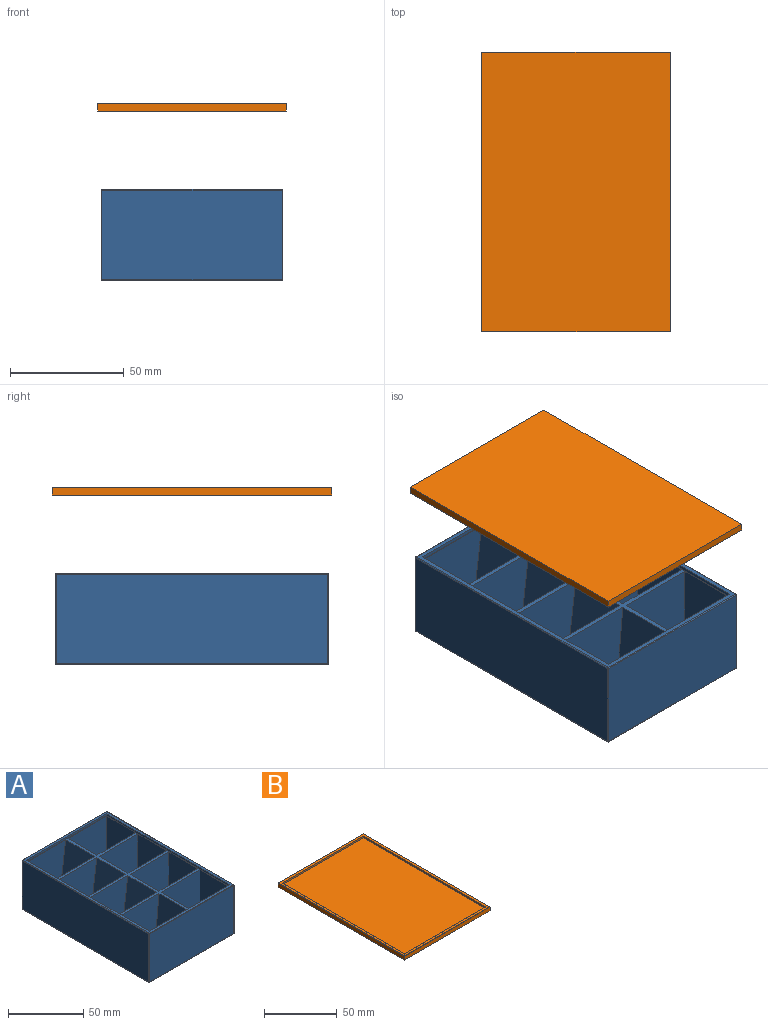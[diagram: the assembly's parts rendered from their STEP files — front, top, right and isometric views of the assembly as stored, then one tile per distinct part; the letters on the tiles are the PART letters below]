
ASSEMBLY  parts=2 mates=1
PART A: 81 faces, bbox 80x120x40 mm
  f0: plane 119.2x79.2mm, normal (0,0,1), area 701.3mm2, adj f9,f10,f19,f20,f27,f28,f29,f30
  f1: plane 79.2x39.2mm, normal (0,-1,0), area 3104.6mm2, adj f14,f19,f22,f25
  f2: plane 119.2x39.2mm, normal (1,0,0), area 4672.6mm2, adj f11,f20,f21,f25
  f3: plane 79.2x39.2mm, normal (0,1,0), area 3104.6mm2, adj f6,f10,f11,f12
  f4: plane 119.2x39.2mm, normal (-1,0,0), area 4672.6mm2, adj f6,f9,f13,f14
  f5: plane 119.2x79.2mm, normal (0,0,-1), area 9440.6mm2, adj f12,f13,f21,f22
  f6: cylinder r=0.4mm len=39.2mm, axis (0,0,1), area 24.6mm2, adj f3,f4,f7,f8
  f7: sphere r=0.4mm, area 0.3mm2, adj f6,f9,f10
  f8: sphere r=0.4mm, area 0.3mm2, adj f6,f12,f13
  f9: cylinder r=0.4mm len=119.2mm, axis (0,1,0), area 74.9mm2, adj f0,f4,f7,f15
  f10: cylinder r=0.4mm len=79.2mm, axis (1,0,0), area 49.8mm2, adj f0,f3,f7,f16
  f11: cylinder r=0.4mm len=39.2mm, axis (0,0,-1), area 24.6mm2, adj f2,f3,f16,f17
  f12: cylinder r=0.4mm len=79.2mm, axis (-1,0,0), area 49.8mm2, adj f3,f5,f8,f17
  f13: cylinder r=0.4mm len=119.2mm, axis (0,-1,0), area 74.9mm2, adj f4,f5,f8,f18
  f14: cylinder r=0.4mm len=39.2mm, axis (0,0,-1), area 24.6mm2, adj f1,f4,f15,f18
  f15: sphere r=0.4mm, area 0.3mm2, adj f9,f14,f19
  f16: sphere r=0.4mm, area 0.3mm2, adj f10,f11,f20
  f17: sphere r=0.4mm, area 0.3mm2, adj f11,f12,f21
  f18: sphere r=0.4mm, area 0.3mm2, adj f13,f14,f22
  f19: cylinder r=0.4mm len=79.2mm, axis (-1,0,0), area 49.8mm2, adj f0,f1,f15,f23
  f20: cylinder r=0.4mm len=119.2mm, axis (0,-1,0), area 74.9mm2, adj f0,f2,f16,f23
  f21: cylinder r=0.4mm len=119.2mm, axis (0,1,0), area 74.9mm2, adj f2,f5,f17,f24
  f22: cylinder r=0.4mm len=79.2mm, axis (1,0,0), area 49.8mm2, adj f1,f5,f18,f24
  f23: sphere r=0.4mm, area 0.3mm2, adj f19,f20,f25
  f24: sphere r=0.4mm, area 0.3mm2, adj f21,f22,f25
  f25: cylinder r=0.4mm len=39.2mm, axis (0,0,1), area 24.6mm2, adj f1,f2,f23,f24
  f26: plane 115.6x75.6mm, normal (0,0,1), area 793.1mm2, adj f27,f28,f29,f30,f32,f33,f34,f35
  f27: plane 115.6x1.5mm, normal (-1,0,0), area 173.4mm2, adj f0,f26,f28,f30
  f28: plane 75.6x1.5mm, normal (0,-1,0), area 113.4mm2, adj f0,f26,f27,f29
  f29: plane 115.6x1.5mm, normal (1,0,0), area 173.4mm2, adj f0,f26,f28,f30
  f30: plane 75.6x1.5mm, normal (0,1,0), area 113.4mm2, adj f0,f26,f27,f29
  f31: plane 31.64x27.25mm, normal (0,0,1), area 862.3mm2, adj f32,f33,f34,f35
  f32: plane 36x27.25mm, normal (-0.99,0,0.13), area 989.3mm2, adj f26,f31,f33,f35
  f33: plane 36.34x36mm, normal (0,1,0), area 1223.6mm2, adj f26,f31,f32,f34
  f34: plane 36x27.25mm, normal (1,0,0), area 981mm2, adj f26,f31,f33,f35
  f35: plane 36.34x36mm, normal (0,-1,0), area 1223.6mm2, adj f26,f31,f32,f34
  f36: plane 31.64x27.25mm, normal (0,0,1), area 862.3mm2, adj f37,f38,f39,f40
  f37: plane 36x27.25mm, normal (-0.99,0,0.13), area 989.3mm2, adj f26,f36,f38,f39
  f38: plane 36.34x36mm, normal (0,-1,0), area 1223.6mm2, adj f26,f36,f37,f40
  f39: plane 36.34x36mm, normal (0,1,0), area 1223.6mm2, adj f26,f36,f37,f40
  f40: plane 36x27.25mm, normal (1,0,0), area 981mm2, adj f26,f36,f38,f39
  f41: plane 31.64x27.25mm, normal (0,0,1), area 862.3mm2, adj f42,f43,f44,f45
  f42: plane 36x27.25mm, normal (-0.99,0,0.13), area 989.3mm2, adj f26,f41,f43,f45
  f43: plane 36.34x36mm, normal (0,-1,0), area 1223.6mm2, adj f26,f41,f42,f44
  f44: plane 36x27.25mm, normal (1,0,0), area 981mm2, adj f26,f41,f43,f45
  f45: plane 36.34x36mm, normal (0,1,0), area 1223.6mm2, adj f26,f41,f42,f44
  f46: plane 33.02x27.25mm, normal (0,0,1), area 899.8mm2, adj f47,f48,f49,f50
  f47: plane 36x27.25mm, normal (-1,0,0.09), area 985.3mm2, adj f26,f46,f48,f50
  f48: plane 36.38x36mm, normal (0,-1,0), area 1249.2mm2, adj f26,f46,f47,f49
  f49: plane 36x27.25mm, normal (1,0,0), area 981mm2, adj f26,f46,f48,f50
  f50: plane 36.38x36mm, normal (0,1,0), area 1249.2mm2, adj f26,f46,f47,f49
  f51: plane 39.97x27.25mm, normal (0,0,1), area 1089.3mm2, adj f52,f53,f54,f55
  f52: plane 36x27.25mm, normal (1,0,-0.09), area 985.3mm2, adj f26,f51,f54,f55
  f53: plane 36x27.25mm, normal (-1,0,0), area 981mm2, adj f26,f51,f54,f55
  f54: plane 39.97x36mm, normal (0,1,0), area 1378.5mm2, adj f26,f51,f52,f53
  f55: plane 39.97x36mm, normal (0,-1,0), area 1378.5mm2, adj f26,f51,f52,f53
  f56: plane 36.5x27.25mm, normal (0,0,1), area 994.6mm2, adj f57,f58,f59,f60
  f57: plane 36.5x36mm, normal (0,1,0), area 1314mm2, adj f26,f56,f58,f60
  f58: plane 36x27.25mm, normal (1,0,0), area 981mm2, adj f26,f56,f57,f59
  f59: plane 36.5x36mm, normal (0,-1,0), area 1314mm2, adj f26,f56,f58,f60
  f60: plane 36x27.25mm, normal (-1,0,0), area 981mm2, adj f26,f56,f57,f59
  f61: plane 36.5x27.25mm, normal (0,0,1), area 994.6mm2, adj f62,f63,f64,f65
  f62: plane 36.5x36mm, normal (0,-1,0), area 1314mm2, adj f26,f61,f63,f65
  f63: plane 36x27.25mm, normal (-1,0,0), area 981mm2, adj f26,f61,f62,f64
  f64: plane 36.5x36mm, normal (0,1,0), area 1314mm2, adj f26,f61,f63,f65
  f65: plane 36x27.25mm, normal (1,0,0), area 981mm2, adj f26,f61,f62,f64
  f66: plane 39.97x27.25mm, normal (0,0,1), area 1089.3mm2, adj f67,f68,f69,f70
  f67: plane 36x27.25mm, normal (1,0,-0.09), area 985.3mm2, adj f26,f66,f69,f70
  f68: plane 36x27.25mm, normal (-1,0,0), area 981mm2, adj f26,f66,f69,f70
  f69: plane 39.97x36mm, normal (0,1,0), area 1378.5mm2, adj f26,f66,f67,f68
  f70: plane 39.97x36mm, normal (0,-1,0), area 1378.5mm2, adj f26,f66,f67,f68
  f71: plane 15.76x1.47mm, normal (0,1,0), area 11.6mm2, adj f72,f73,f75
  f72: plane 27.25x15.76mm, normal (-1,0,0), area 429.4mm2, adj f71,f73,f74,f75
  f73: plane 27.25x1.47mm, normal (0,0,1), area 40.1mm2, adj f71,f72,f74,f75
  f74: plane 15.76x1.47mm, normal (0,-1,0), area 11.6mm2, adj f72,f73,f75
  f75: plane 27.25x15.76mm, normal (1,0,-0.09), area 431.2mm2, adj f71,f72,f73,f74
  f76: plane 27.25x15.76mm, normal (1,0,-0.09), area 431.2mm2, adj f77,f78,f79,f80
  f77: plane 15.76x1.47mm, normal (0,-1,0), area 11.6mm2, adj f76,f79,f80
  f78: plane 15.76x1.47mm, normal (0,1,0), area 11.6mm2, adj f76,f79,f80
  f79: plane 27.25x15.76mm, normal (-1,0,0), area 429.4mm2, adj f76,f77,f78,f80
  f80: plane 27.25x1.47mm, normal (0,0,1), area 40.1mm2, adj f76,f77,f78,f79
PART B: 18 faces, bbox 83x123x3.4 mm
  f0: plane 122.8x82.6mm, normal (0,0,1), area 742.3mm2, adj f1,f11,f12,f13,f14,f15,f16,f17
  f1: plane 83x3.4mm, normal (0,1,0), area 282.2mm2, adj f0,f2,f4,f5,f15,f17
  f2: plane 123x3.2mm, normal (-1,0,0), area 393.6mm2, adj f1,f3,f5,f17
  f3: plane 83x3.2mm, normal (0,-1,0), area 265.6mm2, adj f2,f4,f5,f16
  f4: plane 123x3.2mm, normal (1,0,0), area 393.6mm2, adj f1,f3,f5,f15
  f5: plane 123x83mm, normal (0,0,-1), area 10209mm2, adj f1,f2,f3,f4
  f6: plane 80x1.4mm, normal (0,-1,0), area 112mm2, adj f7,f9,f10,f13
  f7: plane 120x1.4mm, normal (1,0,0), area 168mm2, adj f6,f8,f10,f11
  f8: plane 80x1.4mm, normal (0,1,0), area 112mm2, adj f7,f9,f10,f12
  f9: plane 120x1.4mm, normal (-1,0,0), area 168mm2, adj f6,f8,f10,f14
  f10: plane 120x80mm, normal (0,0,1), area 9600mm2, adj f6,f7,f8,f9
  f11: plane 120x0.5mm, normal (0.71,0,-0.71), area 84.5mm2, adj f0,f7,f12,f13
  f12: plane 80x0.5mm, normal (0,0.71,-0.71), area 56.2mm2, adj f0,f8,f11,f14
  f13: plane 80x0.5mm, normal (0,-0.71,-0.71), area 56.2mm2, adj f0,f6,f11,f14
  f14: plane 120x0.5mm, normal (-0.71,0,-0.71), area 84.5mm2, adj f0,f9,f12,f13
  f15: plane 123x0.2mm, normal (0.71,0,0.71), area 34.8mm2, adj f0,f1,f4,f16
  f16: plane 83x0.2mm, normal (0,-0.71,0.71), area 23.4mm2, adj f0,f3,f15,f17
  f17: plane 123x0.2mm, normal (-0.71,0,0.71), area 34.8mm2, adj f0,f1,f2,f16
PLACE A rot(axis=(0,0,-1),0deg) t=(79.94,-121.06,25.83)mm
PLACE B rot(axis=(0,-1,0),180deg) t=(-0.06,-121.06,101.94)mm
MATE slider B.f5 <-> A.f5  axis (0,0,1) through (39.94,-61.06,103.44)mm
